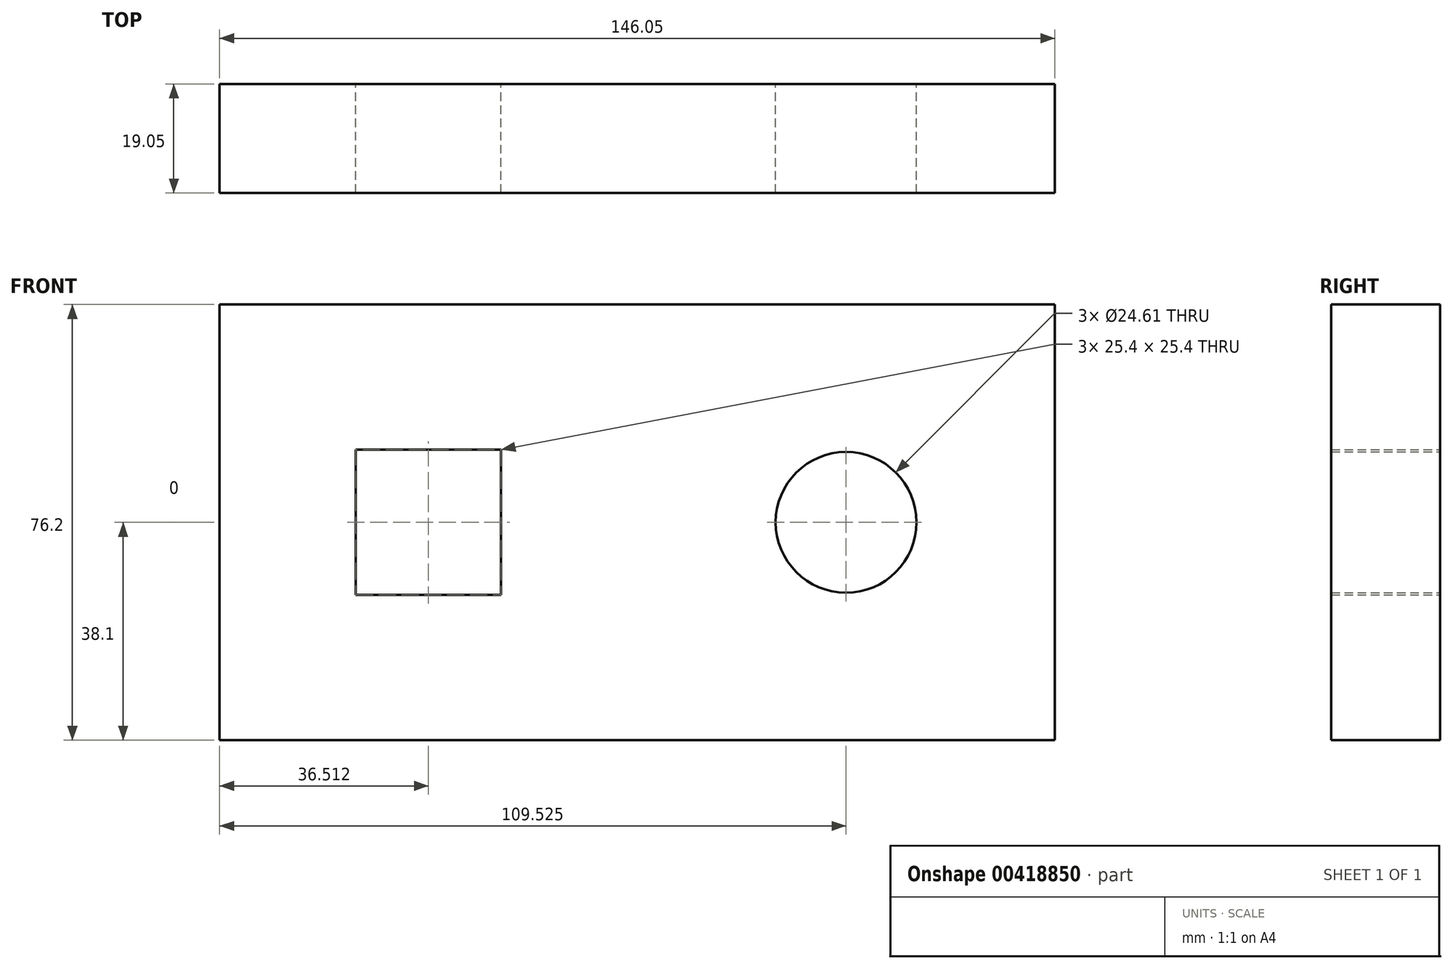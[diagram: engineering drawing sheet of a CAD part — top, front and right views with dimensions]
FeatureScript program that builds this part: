
annotation { "Feature Type Name" : "Feature", "Feature Type Description" : "" }
export const myFeature = defineFeature(function(context is Context, id is Id, definition is map)
    precondition{}
    {
        {
            var Q0;
            Q0=qCreatedBy(makeId("Front.planeOp"),FACE);
            var sketch = newSketch(context, id + "F0", { "sketchPlane" : qUnion([Q0])});
            skLineSegment(sketch, "E0.bottom", {"start": v(74.02, 62.16) * mm, "end": v(-72.03, 62.16) * mm});
            skLineSegment(sketch, "E0.top", {"start": v(74.02, -14.04) * mm, "end": v(-72.03, -14.04) * mm});
            skLineSegment(sketch, "E0.left", {"start": v(74.02, 62.16) * mm, "end": v(74.02, -14.04) * mm});
            skLineSegment(sketch, "E0.right", {"start": v(-72.03, 62.16) * mm, "end": v(-72.03, -14.04) * mm});
            skLineSegment(sketch, "E1.bottom", {"start": v(-48.22, 36.76) * mm, "end": v(-22.82, 36.76) * mm});
            skLineSegment(sketch, "E1.top", {"start": v(-48.22, 11.36) * mm, "end": v(-22.82, 11.36) * mm});
            skLineSegment(sketch, "E1.left", {"start": v(-48.22, 36.76) * mm, "end": v(-48.22, 11.36) * mm});
            skLineSegment(sketch, "E1.right", {"start": v(-22.82, 36.76) * mm, "end": v(-22.82, 11.36) * mm});
            skPoint(sketch, "E1.middle", {"position": v(-35.52, 24.06) * mm});
            skCircle(sketch, "E2", {"center": v(37.5, 24.06) * mm, "radius": 12.3 * mm});
            skSolve(sketch);
        }
        {
            var Q0;
            Q0 = qSketchRegion(id + "F0", true);
            extrude(context, id + "F1", {"entities" : qUnion([Q0]), "depth" : 19.05 * mm});
        }
    });
